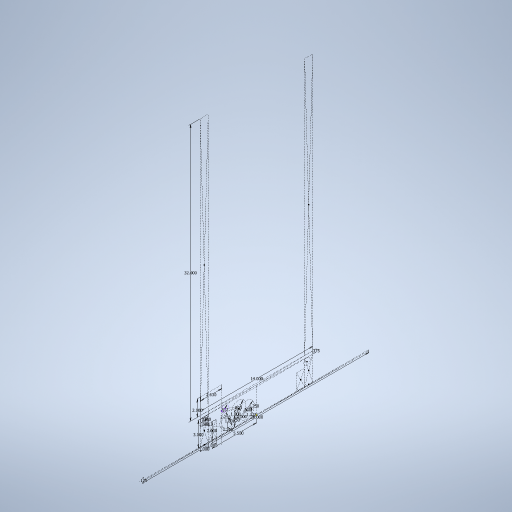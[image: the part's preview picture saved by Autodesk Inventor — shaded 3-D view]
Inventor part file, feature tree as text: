
AUTODESK INVENTOR PART (.ipt)
format: ipt  version: 2023.4 (Build 274418000, 418)  size: 276,480 bytes
history: native  units: in
note: dims shown in document units (in); Inventor stores cm internally (conversion verified against a paired STEP export)
features: sketch x1
ambient origin geometry x8: Origin, YZ Plane, XZ Plane, XY Plane, X Axis, Y Axis, Z Axis, Center Point
feature tree (1):
  sketch  "Sketch1"  dims[d0=0.125in d1=28.0in d2=2.0in d3=1.0in d4=5.5in d5=3.0in d6=1.0in d7=32.0in d8=1.0in d9=0.375in d10=14.0in d11=0.812in d12=0.438in d13=0.3in d15=2.0in d16=0.5in d17=1.8in d18=0.8in d19=1.8in d20=1.125in d22=1.75in d23=2.63in d24=2.0in d25=2.256in d26=1.25in d28=1.25in d29=0.812in]
